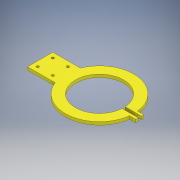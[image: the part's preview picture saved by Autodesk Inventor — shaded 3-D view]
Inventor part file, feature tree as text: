
AUTODESK INVENTOR PART (.ipt)
format: ipt  version: 2018 (Build 220112000, 112)  size: 157,696 bytes
history: native  units: mm
features: extrude x3, sketch x3, other x1
ambient origin geometry x8: Origin, YZ Plane, XZ Plane, XY Plane, X Axis, Y Axis, Z Axis, Center Point
bodies: Body1 (feature_tree)
feature tree (7):
  other  "ソリッド1"
  extrude  "押し出し1"  Depth=96.0mm
  extrude  "押し出し2"  Depth=50.0mm
  extrude  "押し出し3"  Depth=20.0mm
  sketch  "スケッチ2"
  sketch  "スケッチ3"
  sketch  "スケッチ4"
